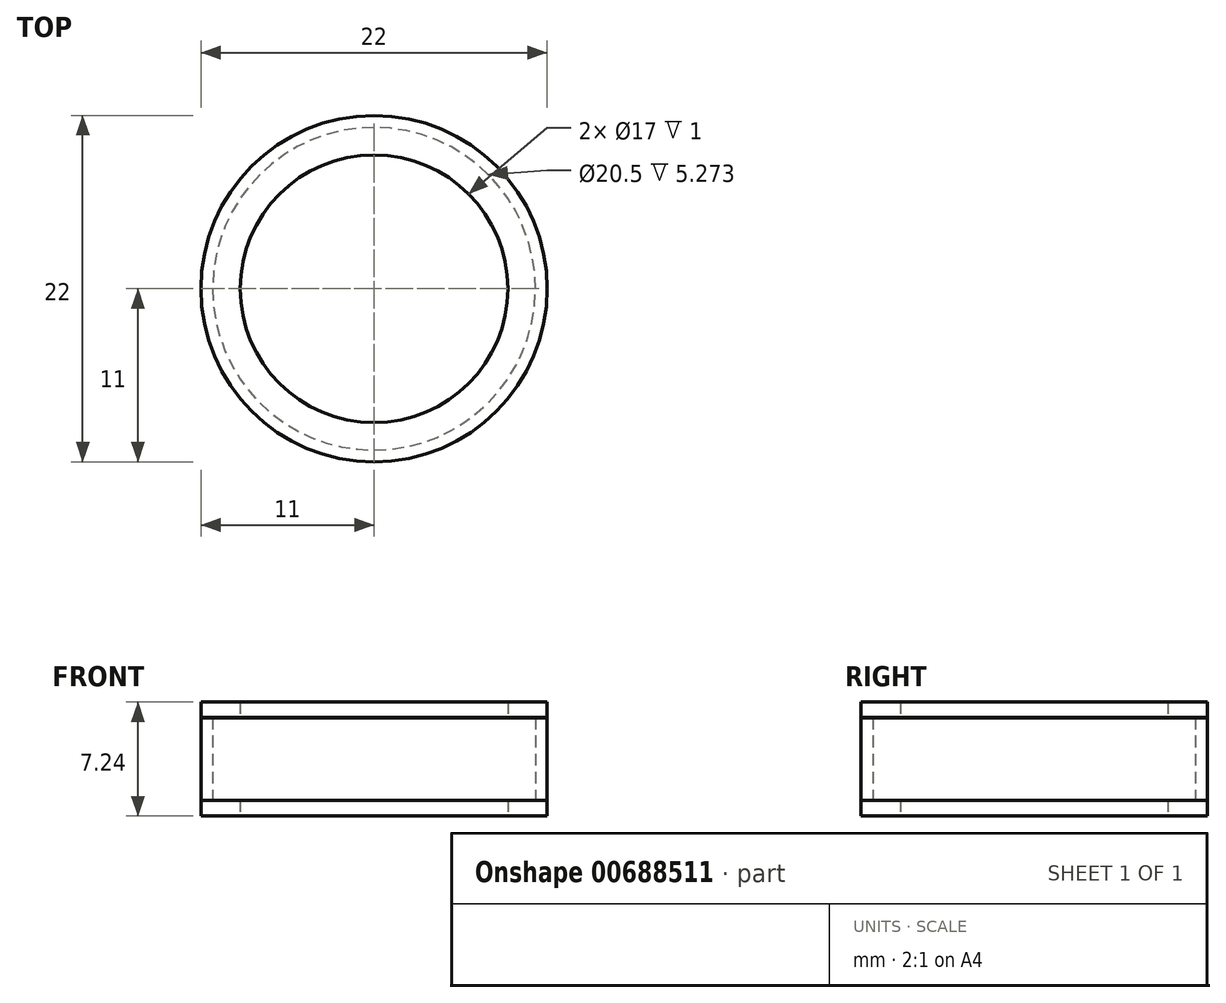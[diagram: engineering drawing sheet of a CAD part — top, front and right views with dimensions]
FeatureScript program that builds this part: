
annotation { "Feature Type Name" : "Feature", "Feature Type Description" : "" }
export const myFeature = defineFeature(function(context is Context, id is Id, definition is map)
    precondition{}
    {
        {
            var Q0;
            Q0=qCreatedBy(makeId("Top.planeOp"),FACE);
            var sketch = newSketch(context, id + "F0", { "sketchPlane" : qUnion([Q0])});
            skCircle(sketch, "E0", {"center": v(0, 0) * mm, "radius": 11 * mm});
            skCircle(sketch, "E1", {"center": v(0, 0) * mm, "radius": 8.5 * mm});
            skSolve(sketch);
        }
        {
            var Q0;
            Q0=qCreatedBy(makeId("Top.planeOp"),FACE);
            cPlane(context, id + "F1", {"entities" : qUnion([Q0]), "cplaneType" : CPlaneType.OFFSET, "offset" : 6.24 * mm, "width" : 152.4 * mm, "height" : 152.4 * mm});
        }
        {
            var Q0;
            Q0=qCreatedBy(id+"F1.planeOp",FACE);
            var sketch = newSketch(context, id + "F2", { "sketchPlane" : qUnion([Q0])});
            skCircle(sketch, "E2", {"center": v(0, 0) * mm, "radius": 8.5 * mm});
            skCircle(sketch, "E3", {"center": v(0, 0) * mm, "radius": 11 * mm});
            skSolve(sketch);
        }
        {
            var Q0;
            Q0=qCreatedBy(makeId("Top.planeOp"),FACE);
            cPlane(context, id + "F3", {"entities" : qUnion([Q0]), "cplaneType" : CPlaneType.OFFSET, "offset" : 3.12 * mm, "width" : 152.4 * mm, "height" : 152.4 * mm});
        }
        {
            var Q0;
            Q0=makeQuery(id+"F2.imprint","IMPRINT",FACE,{"disambiguationData":[TD([[makeQuery(id+"F2.imprint","IMPRINT",EDGE,{"derivedFrom":sQuery(id+"F2.wireOp",EDGE,"E2")}),-1.0]])]});
            var Q1;
            Q1=makeQuery(id+"F0.imprint","IMPRINT",FACE,{"disambiguationData":[TD([[makeQuery(id+"F0.imprint","IMPRINT",EDGE,{"derivedFrom":sQuery(id+"F0.wireOp",EDGE,"E0")}),1.0]])]});
            extrude(context, id + "F4", {"entities" : qUnion([Q0, Q1]), "endBound" : BoundingType.SYMMETRIC, "depth" : 1 * mm, "offsetDistance" : 25.4 * mm});
        }
        {
            var Q0;
            Q0=qCreatedBy(id+"F3.planeOp",FACE);
            var sketch = newSketch(context, id + "F5", { "sketchPlane" : qUnion([Q0])});
            skCircle(sketch, "E4", {"center": v(0, 0) * mm, "radius": 11 * mm});
            skCircle(sketch, "E5", {"center": v(0, 0) * mm, "radius": 10.25 * mm});
            skSolve(sketch);
        }
        {
            var Q0;
            Q0=makeQuery(id+"F5.imprint","IMPRINT",FACE,{"disambiguationData":[TD([[makeQuery(id+"F5.imprint","IMPRINT",EDGE,{"derivedFrom":sQuery(id+"F5.wireOp",EDGE,"E4")}),1.0]])]});
            extrude(context, id + "F6", {"entities" : qUnion([Q0]), "endBound" : BoundingType.SYMMETRIC, "depth" : 5.27 * mm, "offsetDistance" : 25.4 * mm});
        }
    });
